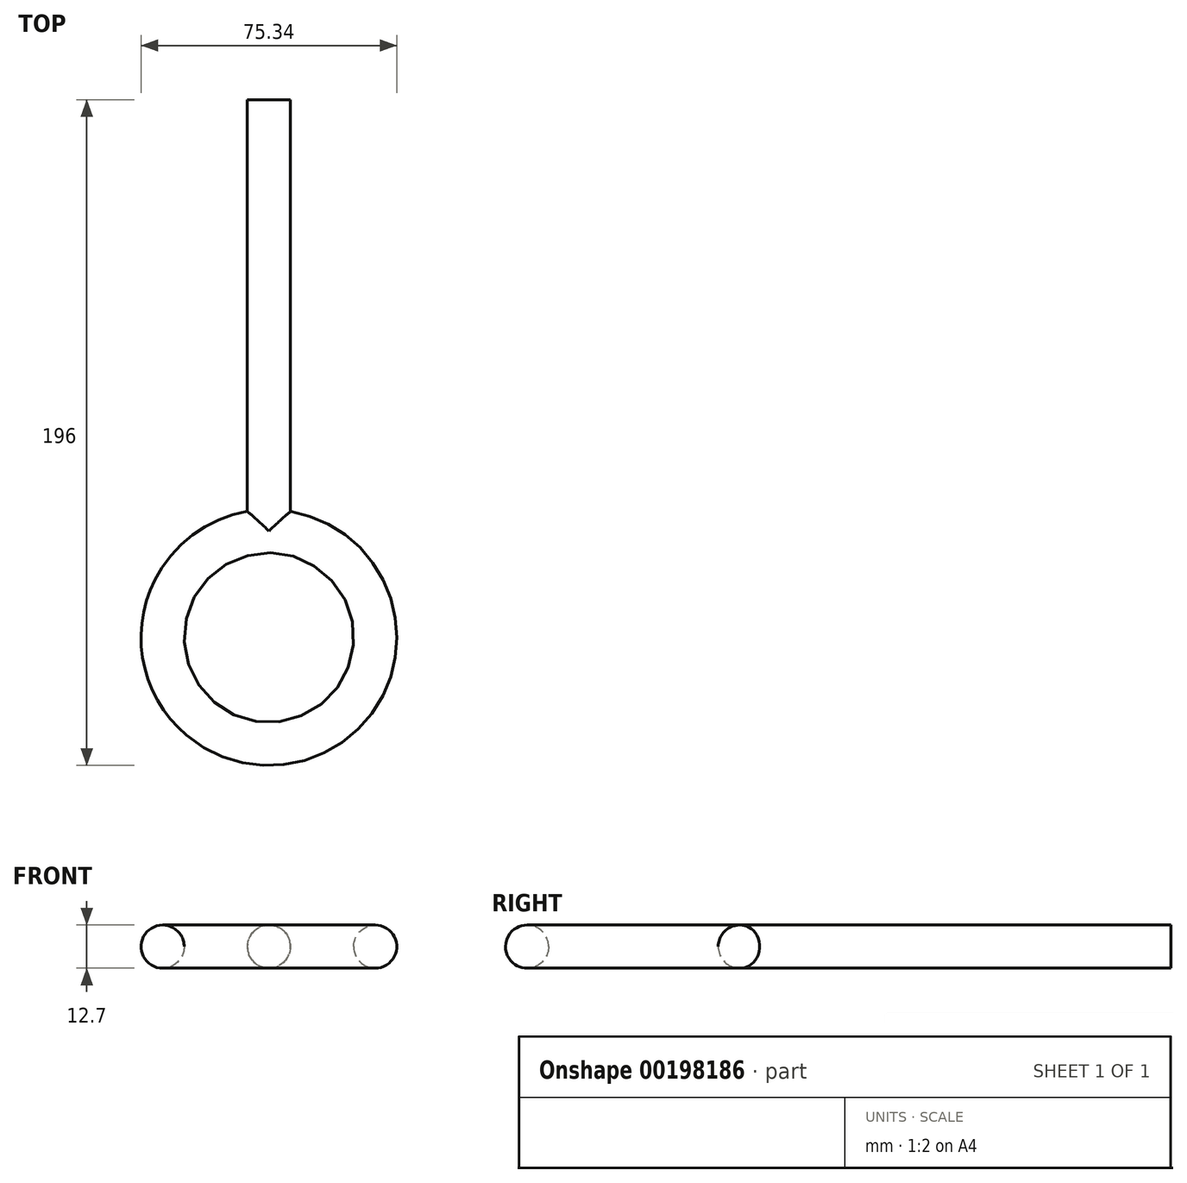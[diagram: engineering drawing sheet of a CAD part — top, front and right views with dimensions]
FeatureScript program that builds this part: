
annotation { "Feature Type Name" : "Feature", "Feature Type Description" : "" }
export const myFeature = defineFeature(function(context is Context, id is Id, definition is map)
    precondition{}
    {
        {
            var Q0;
            Q0=qCreatedBy(makeId("Front.planeOp"),FACE);
            var sketch = newSketch(context, id + "F0", { "sketchPlane" : qUnion([Q0])});
            skCircle(sketch, "E0", {"center": v(0, 0) * mm, "radius": 6.35 * mm});
            skSolve(sketch);
        }
        {
            var Q0;
            Q0=makeQuery(id+"F0.imprint","IMPRINT",FACE,{"disambiguationData":[TD([[makeQuery(id+"F0.imprint","IMPRINT",EDGE,{"derivedFrom":sQuery(id+"F0.wireOp",EDGE,"E0")}),1.0]])]});
            extrude(context, id + "F1", {"entities" : qUnion([Q0]), "endBound" : BoundingType.SYMMETRIC, "depth" : 127 * mm});
        }
        {
            var Q0;
            Q0=qCreatedBy(makeId("Top.planeOp"),FACE);
            var sketch = newSketch(context, id + "F2", { "sketchPlane" : qUnion([Q0])});
            skCircle(sketch, "E1", {"center": v(0, -94.83) * mm, "radius": 31.32 * mm});
            skPoint(sketch, "E1.first.point", {"position": v(0, -63.52) * mm});
            skPoint(sketch, "E1.second.point", {"position": v(0, -126.15) * mm});
            skPoint(sketch, "E1.third.point", {"position": v(-31.32, -94.74) * mm});
            skLineSegment(sketch, "E2", {"start": v(0, -126.15) * mm, "end": v(0, -63.52) * mm});
            skSolve(sketch);
        }
        {
            var Q0;
            Q0=qCreatedBy(makeId("Right.planeOp"),FACE);
            var sketch = newSketch(context, id + "F3", { "sketchPlane" : qUnion([Q0])});
            skCircle(sketch, "E3", {"center": v(-63.52, 0) * mm, "radius": 6.35 * mm});
            skSolve(sketch);
        }
        {
            var Q0;
            Q0=makeQuery(id+"F3.imprint","IMPRINT",FACE,{"disambiguationData":[TD([[makeQuery(id+"F3.imprint","IMPRINT",EDGE,{"derivedFrom":sQuery(id+"F3.wireOp",EDGE,"E3")}),1.0]])]});
            var Q1;
            Q1=sQuery(id+"F2.wireOp",EDGE,"E1");
            sweep(context, id + "F4", {"operationType" : NewBodyOperationType.ADD, "profiles" : qUnion([Q0]), "path" : qUnion([Q1])});
        }
    });
